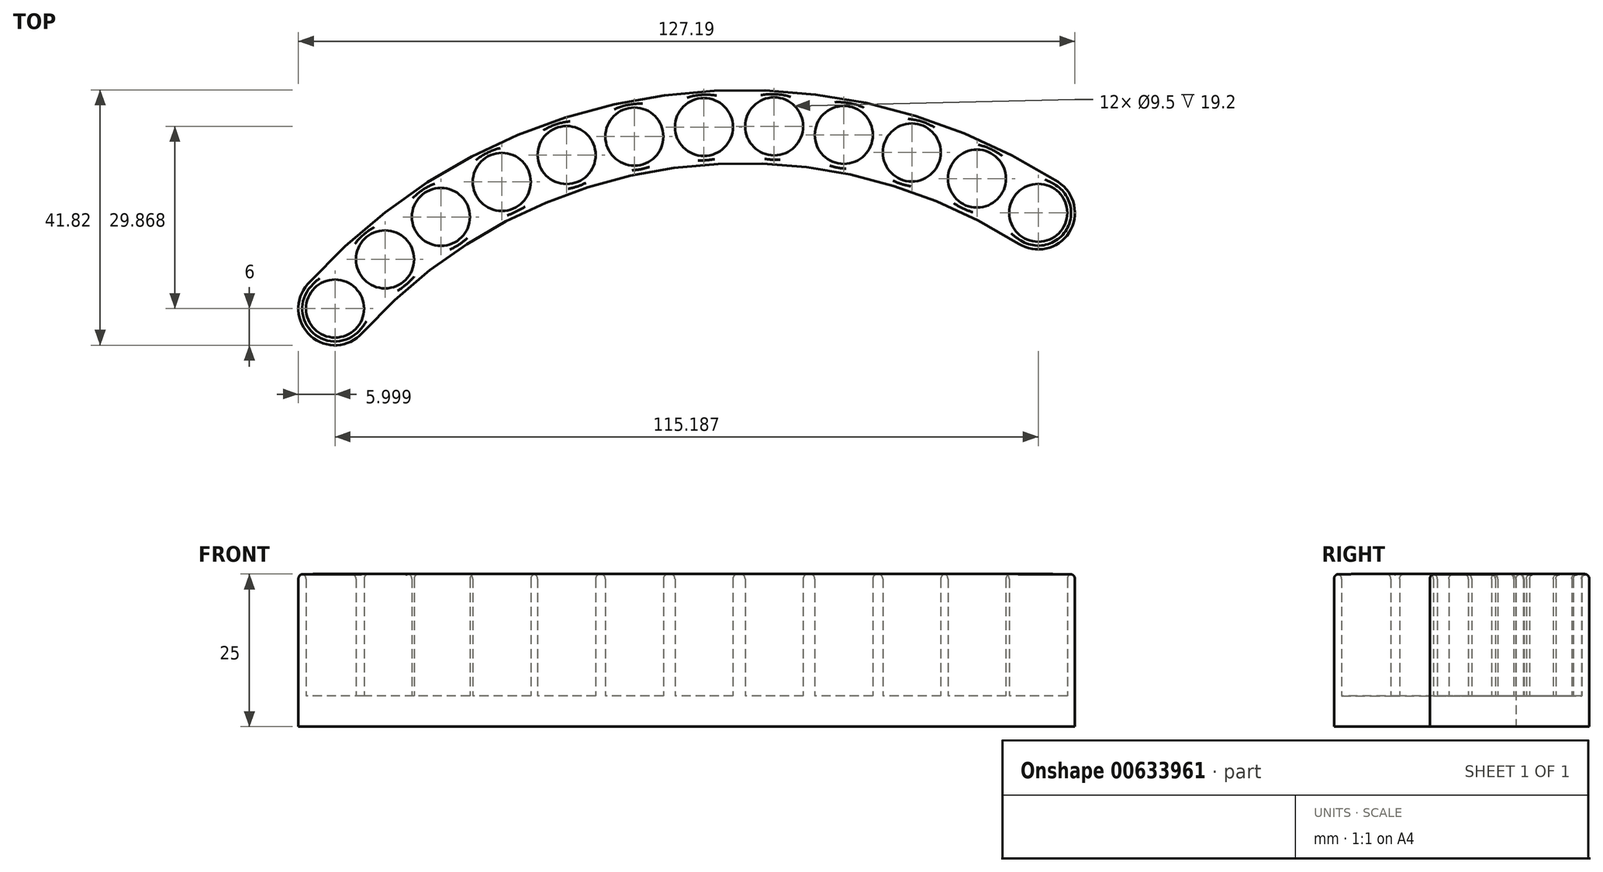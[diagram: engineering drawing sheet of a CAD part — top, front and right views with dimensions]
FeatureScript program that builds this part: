
annotation { "Feature Type Name" : "Feature", "Feature Type Description" : "" }
export const myFeature = defineFeature(function(context is Context, id is Id, definition is map)
    precondition{}
    {
        {
            var Q0;
            Q0=qCreatedBy(makeId("Top.planeOp"),FACE);
            var sketch = newSketch(context, id + "F0", { "sketchPlane" : qUnion([Q0])});
            skPoint(sketch, "E0", {"position": v(0, 30) * mm});
            skCircle(sketch, "E1", {"center": v(-59.6, 8.07) * mm, "radius": 4.75 * mm});
            skCircle(sketch, "E2", {"center": v(-67.8, 0) * mm, "radius": 4.75 * mm});
            skCircle(sketch, "E3", {"center": v(-40.47, 20.76) * mm, "radius": 4.75 * mm});
            skCircle(sketch, "E4", {"center": v(-50.44, 15.03) * mm, "radius": 4.75 * mm});
            skCircle(sketch, "E5", {"center": v(-18.76, 28.19) * mm, "radius": 4.75 * mm});
            skCircle(sketch, "E6", {"center": v(-29.85, 25.17) * mm, "radius": 4.75 * mm});
            skCircle(sketch, "E7", {"center": v(4.14, 29.87) * mm, "radius": 4.75 * mm});
            skCircle(sketch, "E8", {"center": v(-7.36, 29.76) * mm, "radius": 4.75 * mm});
            skCircle(sketch, "E9", {"center": v(26.68, 25.59) * mm, "radius": 4.75 * mm});
            skCircle(sketch, "E10", {"center": v(15.55, 28.47) * mm, "radius": 4.75 * mm});
            skCircle(sketch, "E11", {"center": v(47.4, 15.7) * mm, "radius": 4.75 * mm});
            skCircle(sketch, "E12", {"center": v(37.36, 21.3) * mm, "radius": 4.75 * mm});
            skArc(sketch, "E13.trimOffspring", {"start": v(47.4, 15.7) * mm, "mid": v(-13.08, 29) * mm, "end": v(-67.8, 0) * mm});
            skPoint(sketch, "E14.start.orphan", {"position": v(66.2, 0) * mm});
            skArc(sketch, "E15.0", {"start": v(50.63, 20.75) * mm, "mid": v(-13.89, 34.94) * mm, "end": v(-72.26, 4) * mm});
            skArc(sketch, "E16.0", {"start": v(44.17, 10.64) * mm, "mid": v(-12.27, 23.05) * mm, "end": v(-63.33, -4) * mm});
            skArc(sketch, "E17", {"start": v(44.17, 10.64) * mm, "mid": v(52.45, 12.47) * mm, "end": v(50.63, 20.75) * mm});
            skArc(sketch, "E18", {"start": v(-72.26, 4) * mm, "mid": v(-71.8, -4.47) * mm, "end": v(-63.33, -4) * mm});
            skSolve(sketch);
        }
        {
            var Q0;
            Q0 = qSketchRegion(id + "F0", true);
            extrude(context, id + "F1", {"entities" : qUnion([Q0]), "depth" : 20 * mm, "offsetDistance" : 25 * mm});
        }
        {
            var Q0;
            Q0=makeQuery(id+"F0.imprint","IMPRINT",FACE,{"disambiguationData":[TD([[makeQuery(id+"F0.imprint","IMPRINT",EDGE,{"derivedFrom":sQuery(id+"F0.wireOp",EDGE,"E2")}),-1.0]])]});
            var sketch = newSketch(context, id + "F2", { "sketchPlane" : qUnion([Q0])});
            skSolve(sketch);
        }
        {
            var Q0;
            Q0 = qSketchRegion(id + "F2", true);
            var Q1;
            Q1=makeQuery(id+"F0.imprint","IMPRINT",FACE,{"disambiguationData":[TD([[makeQuery(id+"F0.imprint","IMPRINT",EDGE,{"derivedFrom":sQuery(id+"F0.wireOp",EDGE,"E2")}),-1.0]])]});
            var Q2;
            Q2=makeQuery(id+"F0.imprint","IMPRINT",FACE,{"disambiguationData":[TD([[makeQuery(id+"F0.imprint","IMPRINT",EDGE,{"derivedFrom":sQuery(id+"F0.wireOp",EDGE,"E2")}),1.0]])]});
            var Q3;
            {var subQ0=sQuery(id+"F0.wireOp",EDGE,"E13.trimOffspring");var subQ1=sQuery(id+"F0.wireOp",EDGE,"E1");var subQ2=makeQuery(id+"F0.imprint","INTERSECT",VERTEX,{"disambiguationData":[OD(0.0)],"derivedFrom":[subQ1,subQ0]});Q3=makeQuery(id+"F0.imprint","IMPRINT",FACE,{"disambiguationData":[TD([[makeQuery(id+"F0.imprint","IMPRINT",EDGE,{"disambiguationData":[TD([[subQ2,1.0]])],"derivedFrom":subQ1}),1.0]])]});}
            var Q4;
            {var subQ0=sQuery(id+"F0.wireOp",EDGE,"E13.trimOffspring");var subQ1=sQuery(id+"F0.wireOp",EDGE,"E4");var subQ2=makeQuery(id+"F0.imprint","INTERSECT",VERTEX,{"disambiguationData":[OD(0.0)],"derivedFrom":[subQ1,subQ0]});Q4=makeQuery(id+"F0.imprint","IMPRINT",FACE,{"disambiguationData":[TD([[makeQuery(id+"F0.imprint","IMPRINT",EDGE,{"disambiguationData":[TD([[subQ2,1.0]])],"derivedFrom":subQ1}),1.0]])]});}
            var Q5;
            {var subQ0=sQuery(id+"F0.wireOp",EDGE,"E13.trimOffspring");var subQ1=sQuery(id+"F0.wireOp",EDGE,"E3");var subQ2=makeQuery(id+"F0.imprint","INTERSECT",VERTEX,{"disambiguationData":[OD(0.0)],"derivedFrom":[subQ1,subQ0]});Q5=makeQuery(id+"F0.imprint","IMPRINT",FACE,{"disambiguationData":[TD([[makeQuery(id+"F0.imprint","IMPRINT",EDGE,{"disambiguationData":[TD([[subQ2,1.0]])],"derivedFrom":subQ1}),1.0]])]});}
            var Q6;
            {var subQ0=sQuery(id+"F0.wireOp",EDGE,"E13.trimOffspring");var subQ1=sQuery(id+"F0.wireOp",EDGE,"E6");var subQ2=makeQuery(id+"F0.imprint","INTERSECT",VERTEX,{"disambiguationData":[OD(0.0)],"derivedFrom":[subQ1,subQ0]});Q6=makeQuery(id+"F0.imprint","IMPRINT",FACE,{"disambiguationData":[TD([[makeQuery(id+"F0.imprint","IMPRINT",EDGE,{"disambiguationData":[TD([[subQ2,1.0]])],"derivedFrom":subQ1}),1.0]])]});}
            var Q7;
            {var subQ0=sQuery(id+"F0.wireOp",EDGE,"E13.trimOffspring");var subQ1=sQuery(id+"F0.wireOp",EDGE,"E5");var subQ2=makeQuery(id+"F0.imprint","INTERSECT",VERTEX,{"disambiguationData":[OD(0.0)],"derivedFrom":[subQ1,subQ0]});Q7=makeQuery(id+"F0.imprint","IMPRINT",FACE,{"disambiguationData":[TD([[makeQuery(id+"F0.imprint","IMPRINT",EDGE,{"disambiguationData":[TD([[subQ2,1.0]])],"derivedFrom":subQ1}),1.0]])]});}
            var Q8;
            {var subQ0=sQuery(id+"F0.wireOp",EDGE,"E13.trimOffspring");var subQ1=sQuery(id+"F0.wireOp",EDGE,"E8");var subQ2=makeQuery(id+"F0.imprint","INTERSECT",VERTEX,{"disambiguationData":[OD(0.0)],"derivedFrom":[subQ1,subQ0]});Q8=makeQuery(id+"F0.imprint","IMPRINT",FACE,{"disambiguationData":[TD([[makeQuery(id+"F0.imprint","IMPRINT",EDGE,{"disambiguationData":[TD([[subQ2,1.0]])],"derivedFrom":subQ1}),1.0]])]});}
            var Q9;
            {var subQ0=sQuery(id+"F0.wireOp",EDGE,"E13.trimOffspring");var subQ1=sQuery(id+"F0.wireOp",EDGE,"E7");var subQ2=makeQuery(id+"F0.imprint","INTERSECT",VERTEX,{"disambiguationData":[OD(0.0)],"derivedFrom":[subQ1,subQ0]});Q9=makeQuery(id+"F0.imprint","IMPRINT",FACE,{"disambiguationData":[TD([[makeQuery(id+"F0.imprint","IMPRINT",EDGE,{"disambiguationData":[TD([[subQ2,1.0]])],"derivedFrom":subQ1}),1.0]])]});}
            var Q10;
            {var subQ0=sQuery(id+"F0.wireOp",EDGE,"E13.trimOffspring");var subQ1=sQuery(id+"F0.wireOp",EDGE,"E10");var subQ2=makeQuery(id+"F0.imprint","INTERSECT",VERTEX,{"disambiguationData":[OD(0.0)],"derivedFrom":[subQ1,subQ0]});Q10=makeQuery(id+"F0.imprint","IMPRINT",FACE,{"disambiguationData":[TD([[makeQuery(id+"F0.imprint","IMPRINT",EDGE,{"disambiguationData":[TD([[subQ2,1.0]])],"derivedFrom":subQ1}),1.0]])]});}
            var Q11;
            {var subQ0=sQuery(id+"F0.wireOp",EDGE,"E13.trimOffspring");var subQ1=sQuery(id+"F0.wireOp",EDGE,"E9");var subQ2=makeQuery(id+"F0.imprint","INTERSECT",VERTEX,{"disambiguationData":[OD(0.0)],"derivedFrom":[subQ1,subQ0]});Q11=makeQuery(id+"F0.imprint","IMPRINT",FACE,{"disambiguationData":[TD([[makeQuery(id+"F0.imprint","IMPRINT",EDGE,{"disambiguationData":[TD([[subQ2,1.0]])],"derivedFrom":subQ1}),1.0]])]});}
            var Q12;
            {var subQ0=sQuery(id+"F0.wireOp",EDGE,"E13.trimOffspring");var subQ1=sQuery(id+"F0.wireOp",EDGE,"E12");var subQ2=makeQuery(id+"F0.imprint","INTERSECT",VERTEX,{"disambiguationData":[OD(0.0)],"derivedFrom":[subQ1,subQ0]});Q12=makeQuery(id+"F0.imprint","IMPRINT",FACE,{"disambiguationData":[TD([[makeQuery(id+"F0.imprint","IMPRINT",EDGE,{"disambiguationData":[TD([[subQ2,1.0]])],"derivedFrom":subQ1}),1.0]])]});}
            var Q13;
            Q13=makeQuery(id+"F0.imprint","IMPRINT",FACE,{"disambiguationData":[TD([[makeQuery(id+"F0.imprint","IMPRINT",EDGE,{"derivedFrom":sQuery(id+"F0.wireOp",EDGE,"E11")}),1.0]])]});
            var Q14;
            {var subQ0=sQuery(id+"F0.wireOp",EDGE,"E13.trimOffspring");var subQ1=sQuery(id+"F0.wireOp",EDGE,"E1");var subQ2=makeQuery(id+"F0.imprint","INTERSECT",VERTEX,{"disambiguationData":[OD(0.0)],"derivedFrom":[subQ1,subQ0]});Q14=makeQuery(id+"F0.imprint","IMPRINT",FACE,{"disambiguationData":[TD([[makeQuery(id+"F0.imprint","IMPRINT",EDGE,{"disambiguationData":[TD([[subQ2,-1.0]])],"derivedFrom":subQ1}),1.0]])]});}
            var Q15;
            {var subQ0=sQuery(id+"F0.wireOp",EDGE,"E13.trimOffspring");var subQ1=sQuery(id+"F0.wireOp",EDGE,"E4");var subQ2=makeQuery(id+"F0.imprint","INTERSECT",VERTEX,{"disambiguationData":[OD(0.0)],"derivedFrom":[subQ1,subQ0]});Q15=makeQuery(id+"F0.imprint","IMPRINT",FACE,{"disambiguationData":[TD([[makeQuery(id+"F0.imprint","IMPRINT",EDGE,{"disambiguationData":[TD([[subQ2,-1.0]])],"derivedFrom":subQ1}),1.0]])]});}
            var Q16;
            {var subQ0=sQuery(id+"F0.wireOp",EDGE,"E13.trimOffspring");var subQ1=sQuery(id+"F0.wireOp",EDGE,"E3");var subQ2=makeQuery(id+"F0.imprint","INTERSECT",VERTEX,{"disambiguationData":[OD(0.0)],"derivedFrom":[subQ1,subQ0]});Q16=makeQuery(id+"F0.imprint","IMPRINT",FACE,{"disambiguationData":[TD([[makeQuery(id+"F0.imprint","IMPRINT",EDGE,{"disambiguationData":[TD([[subQ2,-1.0]])],"derivedFrom":subQ1}),1.0]])]});}
            var Q17;
            {var subQ0=sQuery(id+"F0.wireOp",EDGE,"E13.trimOffspring");var subQ1=sQuery(id+"F0.wireOp",EDGE,"E6");var subQ2=makeQuery(id+"F0.imprint","INTERSECT",VERTEX,{"disambiguationData":[OD(0.0)],"derivedFrom":[subQ1,subQ0]});Q17=makeQuery(id+"F0.imprint","IMPRINT",FACE,{"disambiguationData":[TD([[makeQuery(id+"F0.imprint","IMPRINT",EDGE,{"disambiguationData":[TD([[subQ2,-1.0]])],"derivedFrom":subQ1}),1.0]])]});}
            var Q18;
            {var subQ0=sQuery(id+"F0.wireOp",EDGE,"E13.trimOffspring");var subQ1=sQuery(id+"F0.wireOp",EDGE,"E5");var subQ2=makeQuery(id+"F0.imprint","INTERSECT",VERTEX,{"disambiguationData":[OD(0.0)],"derivedFrom":[subQ1,subQ0]});Q18=makeQuery(id+"F0.imprint","IMPRINT",FACE,{"disambiguationData":[TD([[makeQuery(id+"F0.imprint","IMPRINT",EDGE,{"disambiguationData":[TD([[subQ2,-1.0]])],"derivedFrom":subQ1}),1.0]])]});}
            var Q19;
            {var subQ0=sQuery(id+"F0.wireOp",EDGE,"E13.trimOffspring");var subQ1=sQuery(id+"F0.wireOp",EDGE,"E8");var subQ2=makeQuery(id+"F0.imprint","INTERSECT",VERTEX,{"disambiguationData":[OD(0.0)],"derivedFrom":[subQ1,subQ0]});Q19=makeQuery(id+"F0.imprint","IMPRINT",FACE,{"disambiguationData":[TD([[makeQuery(id+"F0.imprint","IMPRINT",EDGE,{"disambiguationData":[TD([[subQ2,-1.0]])],"derivedFrom":subQ1}),1.0]])]});}
            var Q20;
            {var subQ0=sQuery(id+"F0.wireOp",EDGE,"E13.trimOffspring");var subQ1=sQuery(id+"F0.wireOp",EDGE,"E7");var subQ2=makeQuery(id+"F0.imprint","INTERSECT",VERTEX,{"disambiguationData":[OD(0.0)],"derivedFrom":[subQ1,subQ0]});Q20=makeQuery(id+"F0.imprint","IMPRINT",FACE,{"disambiguationData":[TD([[makeQuery(id+"F0.imprint","IMPRINT",EDGE,{"disambiguationData":[TD([[subQ2,-1.0]])],"derivedFrom":subQ1}),1.0]])]});}
            var Q21;
            {var subQ0=sQuery(id+"F0.wireOp",EDGE,"E13.trimOffspring");var subQ1=sQuery(id+"F0.wireOp",EDGE,"E10");var subQ2=makeQuery(id+"F0.imprint","INTERSECT",VERTEX,{"disambiguationData":[OD(0.0)],"derivedFrom":[subQ1,subQ0]});Q21=makeQuery(id+"F0.imprint","IMPRINT",FACE,{"disambiguationData":[TD([[makeQuery(id+"F0.imprint","IMPRINT",EDGE,{"disambiguationData":[TD([[subQ2,-1.0]])],"derivedFrom":subQ1}),1.0]])]});}
            var Q22;
            {var subQ0=sQuery(id+"F0.wireOp",EDGE,"E13.trimOffspring");var subQ1=sQuery(id+"F0.wireOp",EDGE,"E9");var subQ2=makeQuery(id+"F0.imprint","INTERSECT",VERTEX,{"disambiguationData":[OD(0.0)],"derivedFrom":[subQ1,subQ0]});Q22=makeQuery(id+"F0.imprint","IMPRINT",FACE,{"disambiguationData":[TD([[makeQuery(id+"F0.imprint","IMPRINT",EDGE,{"disambiguationData":[TD([[subQ2,-1.0]])],"derivedFrom":subQ1}),1.0]])]});}
            var Q23;
            {var subQ0=sQuery(id+"F0.wireOp",EDGE,"E13.trimOffspring");var subQ1=sQuery(id+"F0.wireOp",EDGE,"E12");var subQ2=makeQuery(id+"F0.imprint","INTERSECT",VERTEX,{"disambiguationData":[OD(0.0)],"derivedFrom":[subQ1,subQ0]});Q23=makeQuery(id+"F0.imprint","IMPRINT",FACE,{"disambiguationData":[TD([[makeQuery(id+"F0.imprint","IMPRINT",EDGE,{"disambiguationData":[TD([[subQ2,-1.0]])],"derivedFrom":subQ1}),1.0]])]});}
            extrude(context, id + "F3", {"entities" : qUnion([Q0, Q1, Q2, Q3, Q4, Q5, Q6, Q7, Q8, Q9, Q10, Q11, Q12, Q13, Q14, Q15, Q16, Q17, Q18, Q19, Q20, Q21, Q22, Q23]), "operationType" : NewBodyOperationType.ADD, "oppositeDirection" : true, "depth" : 5 * mm, "offsetDistance" : 25 * mm});
        }
        {
            var Q0;
            Q0=makeQuery(id+"F1.opExtrude","CAP_FACE",FACE,{"disambiguationData":[OSD([sQuery(id+"F0.wireOp",EDGE,"E1"),sQuery(id+"F0.wireOp",EDGE,"E2"),sQuery(id+"F0.wireOp",EDGE,"E3"),sQuery(id+"F0.wireOp",EDGE,"E4"),sQuery(id+"F0.wireOp",EDGE,"E5"),sQuery(id+"F0.wireOp",EDGE,"E6"),sQuery(id+"F0.wireOp",EDGE,"E7"),sQuery(id+"F0.wireOp",EDGE,"E8"),sQuery(id+"F0.wireOp",EDGE,"E9"),sQuery(id+"F0.wireOp",EDGE,"E10"),sQuery(id+"F0.wireOp",EDGE,"E11"),sQuery(id+"F0.wireOp",EDGE,"E12"),sQuery(id+"F0.wireOp",EDGE,"E15.0"),sQuery(id+"F0.wireOp",EDGE,"E16.0"),sQuery(id+"F0.wireOp",EDGE,"E17"),sQuery(id+"F0.wireOp",EDGE,"E18")])],"isStart":false});
            fillet(context, id + "F4", {"entities" : qUnion([Q0]), "radius" : 0.8 * mm, "tangentPropagation" : true, "allowEdgeOverflow" : false});
        }
    });
